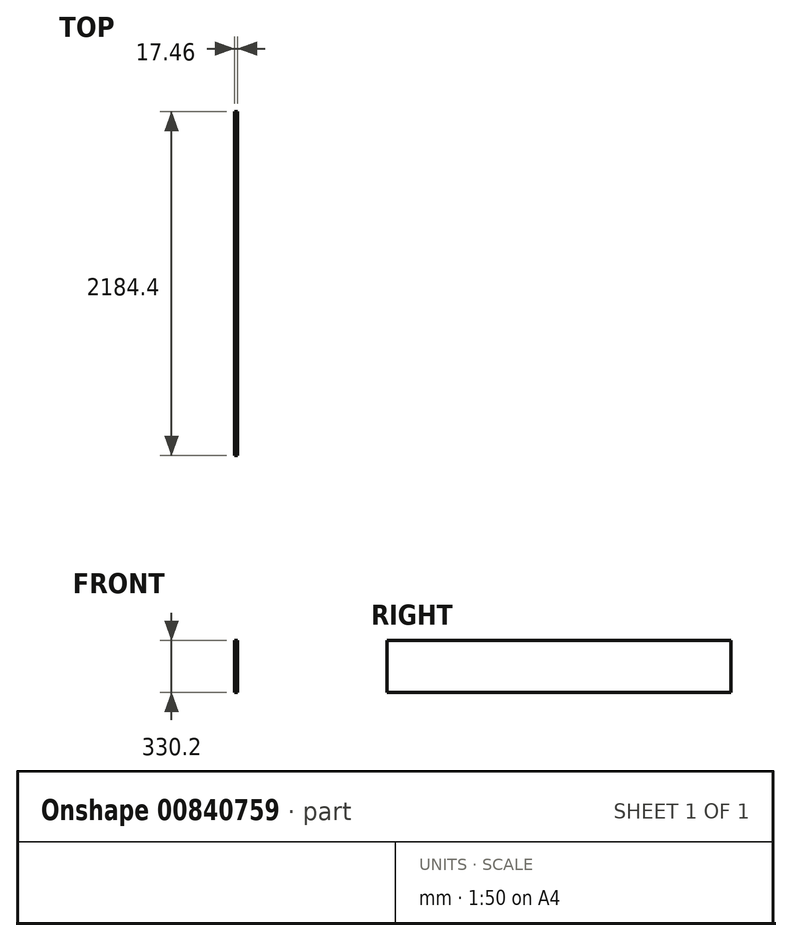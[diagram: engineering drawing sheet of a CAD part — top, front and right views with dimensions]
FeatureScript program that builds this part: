
annotation { "Feature Type Name" : "Feature", "Feature Type Description" : "" }
export const myFeature = defineFeature(function(context is Context, id is Id, definition is map)
    precondition{}
    {
        {
            var Q0;
            Q0=qCreatedBy(makeId("Right.planeOp"),FACE);
            var sketch = newSketch(context, id + "F0", { "sketchPlane" : qUnion([Q0])});
            skLineSegment(sketch, "E0.bottom", {"start": v(-1109.8, -472.62) * mm, "end": v(1074.6, -472.62) * mm});
            skLineSegment(sketch, "E0.top", {"start": v(-1109.8, -802.82) * mm, "end": v(1074.6, -802.82) * mm});
            skLineSegment(sketch, "E0.left", {"start": v(-1109.8, -472.62) * mm, "end": v(-1109.8, -802.82) * mm});
            skLineSegment(sketch, "E0.right", {"start": v(1074.6, -472.62) * mm, "end": v(1074.6, -802.82) * mm});
            skSolve(sketch);
        }
        {
            var Q0;
            Q0=makeQuery(id+"F0.imprint","IMPRINT",FACE,{"disambiguationData":[TD([[makeQuery(id+"F0.imprint","IMPRINT",EDGE,{"derivedFrom":sQuery(id+"F0.wireOp",EDGE,"E0.bottom")}),-1.0]])]});
            extrude(context, id + "F1", {"entities" : qUnion([Q0]), "depth" : 17.46 * mm, "offsetDistance" : 25.4 * mm});
        }
    });
